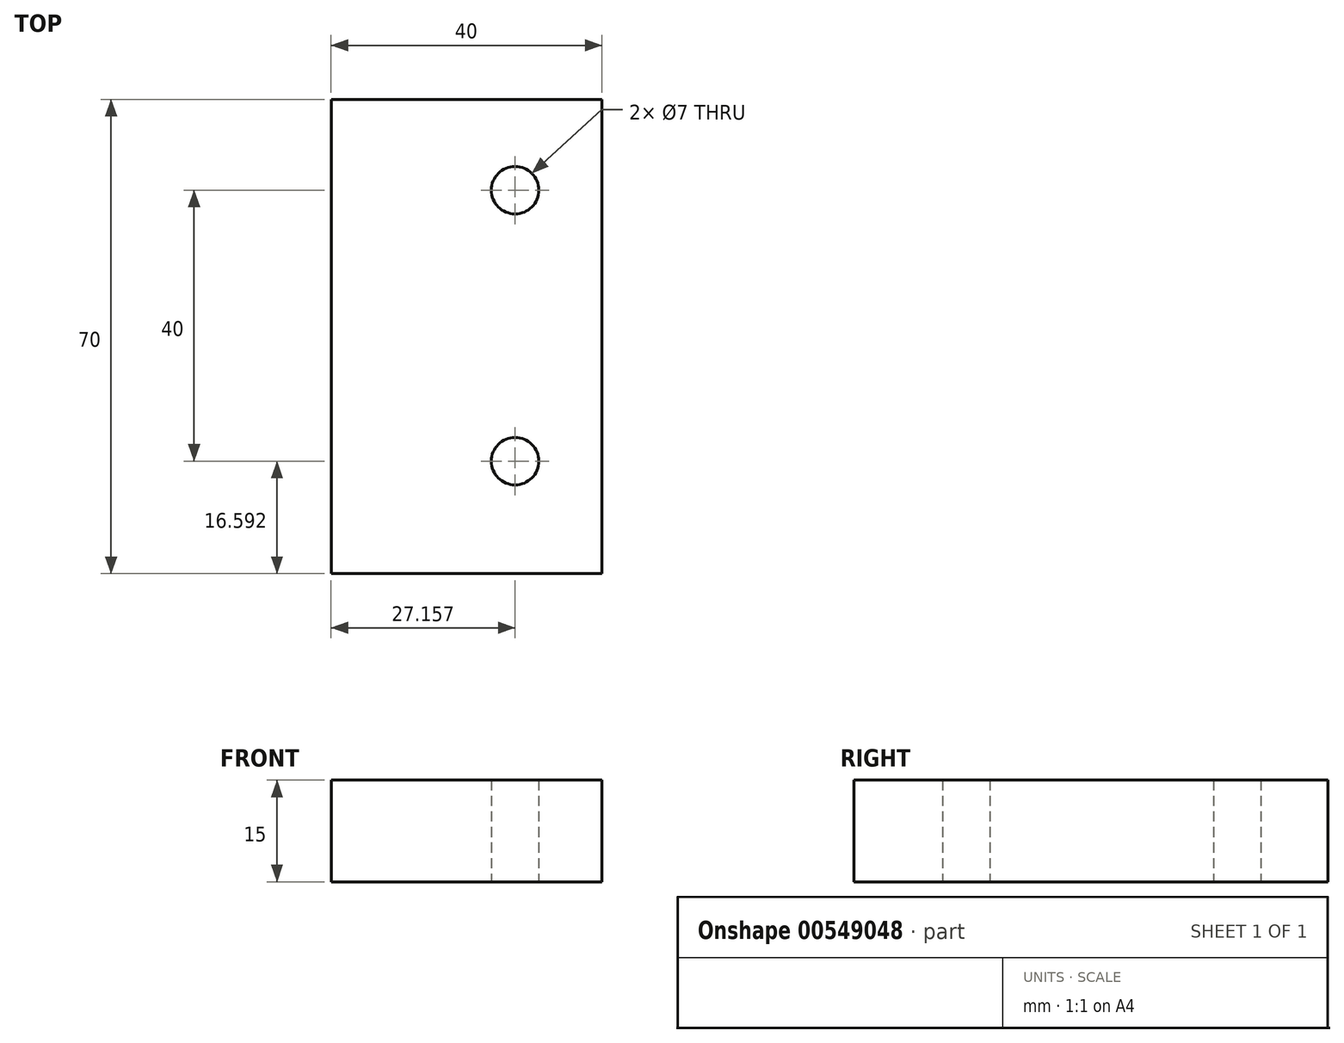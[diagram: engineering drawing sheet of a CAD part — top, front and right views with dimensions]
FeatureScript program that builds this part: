
annotation { "Feature Type Name" : "Feature", "Feature Type Description" : "" }
export const myFeature = defineFeature(function(context is Context, id is Id, definition is map)
    precondition{}
    {
        {
            var Q0;
            Q0=qCreatedBy(makeId("Top.planeOp"),FACE);
            var sketch = newSketch(context, id + "F0", { "sketchPlane" : qUnion([Q0])});
            skLineSegment(sketch, "E0.bottom", {"start": v(-36, 35.54) * mm, "end": v(4, 35.54) * mm});
            skLineSegment(sketch, "E0.top", {"start": v(-36, -34.46) * mm, "end": v(4, -34.46) * mm});
            skLineSegment(sketch, "E0.left", {"start": v(-36, 35.54) * mm, "end": v(-36, -34.46) * mm});
            skLineSegment(sketch, "E0.right", {"start": v(4, 35.54) * mm, "end": v(4, -34.46) * mm});
            skCircle(sketch, "E1", {"center": v(-8.85, 22.13) * mm, "radius": 3.5 * mm});
            skCircle(sketch, "E2", {"center": v(-8.85, -17.87) * mm, "radius": 3.5 * mm});
            skSolve(sketch);
        }
        {
            var Q0;
            Q0=makeQuery(id+"F0.imprint","IMPRINT",FACE,{"disambiguationData":[TD([[makeQuery(id+"F0.imprint","IMPRINT",EDGE,{"derivedFrom":sQuery(id+"F0.wireOp",EDGE,"E0.bottom")}),-1.0]])]});
            extrude(context, id + "F1", {"entities" : qUnion([Q0]), "endBound" : BoundingType.SYMMETRIC, "depth" : 15 * mm, "offsetDistance" : 25 * mm});
        }
    });
